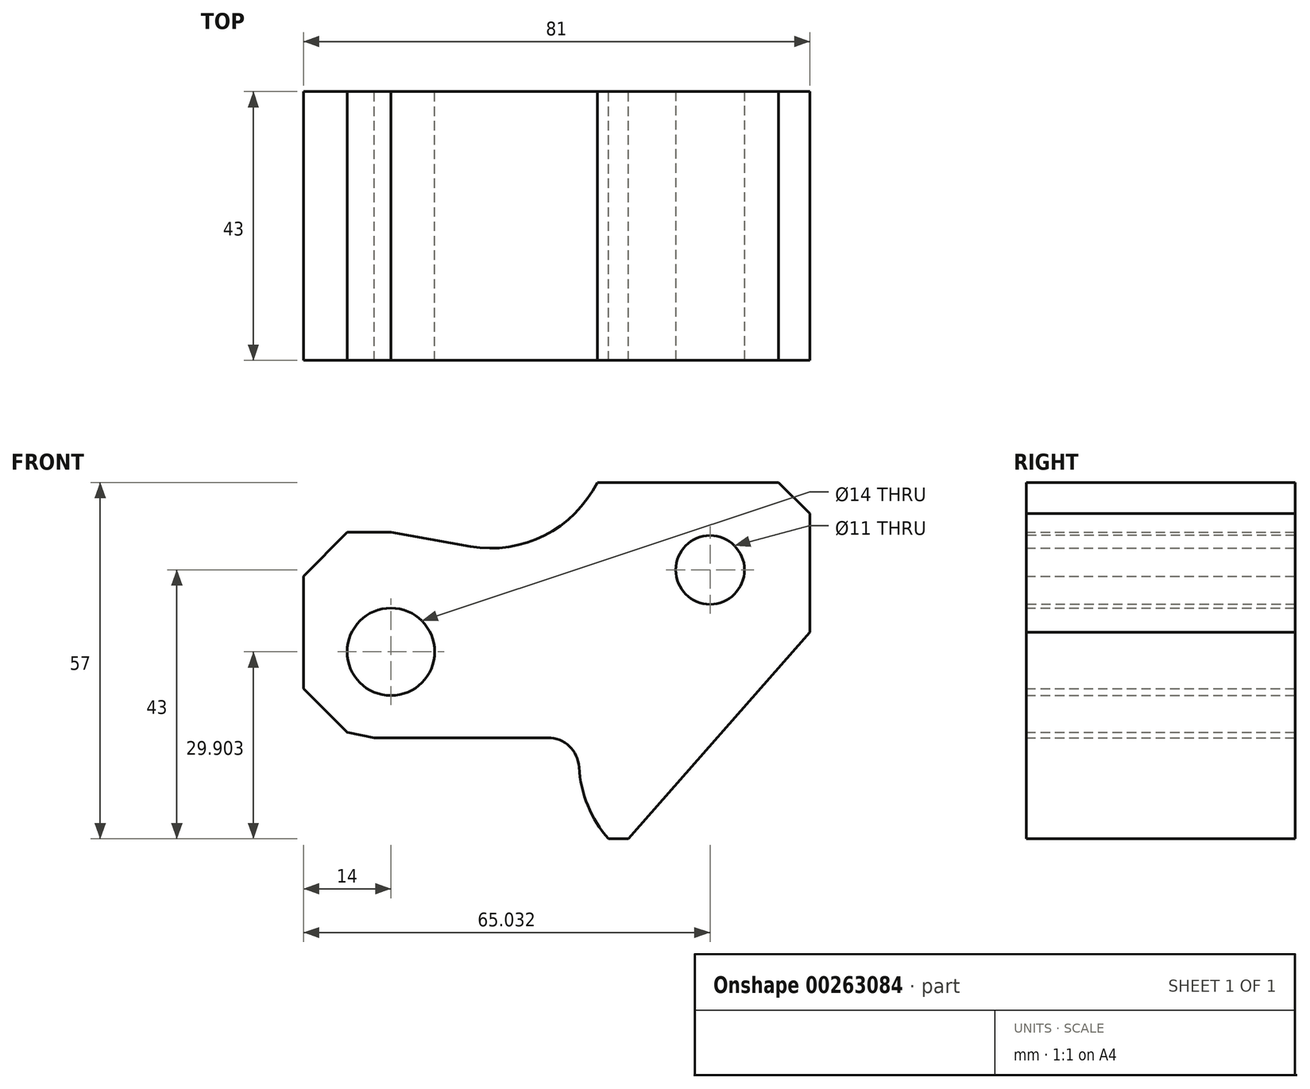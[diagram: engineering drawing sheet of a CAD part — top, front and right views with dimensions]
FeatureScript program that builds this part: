
annotation { "Feature Type Name" : "Feature", "Feature Type Description" : "" }
export const myFeature = defineFeature(function(context is Context, id is Id, definition is map)
    precondition{}
    {
        {
            var Q0;
            Q0=qCreatedBy(makeId("Front.planeOp"),FACE);
            var sketch = newSketch(context, id + "F0", { "sketchPlane" : qUnion([Q0])});
            skLineSegment(sketch, "E0", {"start": v(0, 0) * mm, "end": v(-29, -33) * mm});
            skLineSegment(sketch, "E1", {"start": v(-5, 24) * mm, "end": v(0, 19) * mm});
            skLineSegment(sketch, "E2", {"start": v(0, 19) * mm, "end": v(0, 0) * mm});
            skLineSegment(sketch, "E3", {"start": v(-34, 24) * mm, "end": v(-5, 24) * mm});
            skLineSegment(sketch, "E4", {"start": v(-74, 16) * mm, "end": v(-81, 9) * mm});
            skLineSegment(sketch, "E5", {"start": v(-74, 16) * mm, "end": v(-67, 16) * mm});
            skLineSegment(sketch, "E6", {"start": v(-81, 9) * mm, "end": v(-81, 0) * mm});
            skLineSegment(sketch, "E7", {"start": v(-74, -16) * mm, "end": v(-69.67, -16.84) * mm});
            skLineSegment(sketch, "E8", {"start": v(-81, 0) * mm, "end": v(-81, -9) * mm});
            skLineSegment(sketch, "E9", {"start": v(-74, -16) * mm, "end": v(-81, -9) * mm});
            skLineSegment(sketch, "E10", {"start": v(-67, 16) * mm, "end": v(-54.3, 13.76) * mm});
            skArc(sketch, "E11", {"start": v(-54.3, 13.76) * mm, "mid": v(-42.45, 15.5) * mm, "end": v(-34, 24) * mm});
            skLineSegment(sketch, "E12", {"start": v(-69.67, -16.84) * mm, "end": v(-67, -3.1) * mm});
            skCircle(sketch, "E13", {"center": v(-67, -3.1) * mm, "radius": 7 * mm});
            skLineSegment(sketch, "E14", {"start": v(-69.67, -16.84) * mm, "end": v(-41.91, -16.84) * mm});
            skLineSegment(sketch, "E15", {"start": v(-29, -33) * mm, "end": v(-32.2, -33) * mm});
            skArc(sketch, "E16", {"start": v(-36.92, -21.55) * mm, "mid": v(-35.52, -27.67) * mm, "end": v(-32.2, -33) * mm});
            skPoint(sketch, "E17.visualSharp", {"position": v(-36.61, -16.84) * mm});
            skArc(sketch, "E17.filletArc", {"start": v(-36.92, -21.55) * mm, "mid": v(-38.48, -18.2) * mm, "end": v(-41.91, -16.84) * mm});
            skSolve(sketch);
        }
        {
            var Q0;
            Q0=makeQuery(id+"F0.imprint","IMPRINT",FACE,{"disambiguationData":[TD([[makeQuery(id+"F0.imprint","IMPRINT",EDGE,{"derivedFrom":sQuery(id+"F0.wireOp",EDGE,"E0")}),-1.0]])]});
            extrude(context, id + "F1", {"entities" : qUnion([Q0]), "depth" : 43 * mm});
        }
        {
            var Q0;
            Q0=makeQuery(id+"F1.opExtrude","CAP_FACE",FACE,{"disambiguationData":[OSD([sQuery(id+"F0.wireOp",EDGE,"E0"),sQuery(id+"F0.wireOp",EDGE,"E1"),sQuery(id+"F0.wireOp",EDGE,"E2"),sQuery(id+"F0.wireOp",EDGE,"E3"),sQuery(id+"F0.wireOp",EDGE,"E4"),sQuery(id+"F0.wireOp",EDGE,"E5"),sQuery(id+"F0.wireOp",EDGE,"E6"),sQuery(id+"F0.wireOp",EDGE,"E7"),sQuery(id+"F0.wireOp",EDGE,"E8"),sQuery(id+"F0.wireOp",EDGE,"E9"),sQuery(id+"F0.wireOp",EDGE,"E10"),sQuery(id+"F0.wireOp",EDGE,"E11"),sQuery(id+"F0.wireOp",EDGE,"E13"),sQuery(id+"F0.wireOp",EDGE,"E14"),sQuery(id+"F0.wireOp",EDGE,"E15"),sQuery(id+"F0.wireOp",EDGE,"E16")])],"isStart":false});
            var sketch = newSketch(context, id + "F2", { "sketchPlane" : qUnion([Q0])});
            skCircle(sketch, "E18", {"center": v(-15.97, 10) * mm, "radius": 5.5 * mm});
            skSolve(sketch);
        }
        {
            var Q0;
            Q0=makeQuery(id+"F2.imprint","IMPRINT",FACE,{"disambiguationData":[TD([[makeQuery(id+"F2.imprint","IMPRINT",EDGE,{"derivedFrom":sQuery(id+"F2.wireOp",EDGE,"E18")}),1.0]])]});
            var Q1;
            Q1=sQuery(id+"F2.wireOp",EDGE,"E18");
            extrude(context, id + "F3", {"entities" : qUnion([Q0]), "operationType" : NewBodyOperationType.REMOVE, "surfaceEntities" : qUnion([Q1]), "endBound" : BoundingType.THROUGH_ALL, "oppositeDirection" : true, "depth" : 25 * mm});
        }
    });
